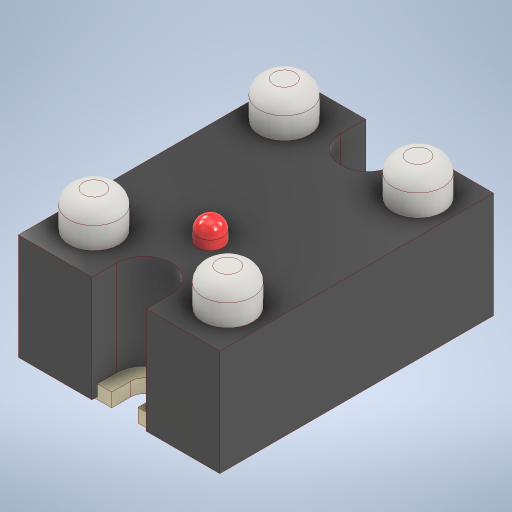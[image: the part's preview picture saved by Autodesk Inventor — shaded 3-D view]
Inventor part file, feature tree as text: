
AUTODESK INVENTOR PART (.ipt)
format: ipt  version: 2023 (Build 270158030, 158C)  size: 387,072 bytes
history: native  units: mm
features: other x4, extrude x4, sketch x4, fillet x2, plane x1, projected_geometry x1
ambient origin geometry x8: Origin, YZ Plane, XZ Plane, XY Plane, X Axis, Y Axis, Z Axis, Center Point
bodies: Body1 (feature_tree), Body2 (feature_tree), Body3 (feature_tree), Body4 (feature_tree)
feature tree (16):
  other  "plate"
  extrude  "Extrusion1"  Depth=26.2mm
  plane  "Work Plane1"
  extrude  "Extrusion2"  Depth=1.9mm TaperAngle=0.0deg
  extrude  "Extrusion3"  Depth=3.64mm
  fillet  "Fillet1"  Radius=3.64mm
  extrude  "Extrusion4"  Depth=36.2mm
  fillet  "Fillet2"  Radius=18.1mm
  sketch  "Sketch1"  dims[d0=36.2mm d1=26.2mm d2=13.1mm]
  sketch  "Sketch2"  dims[d3=18.1mm d4=1.9mm d5=0.0mm]
  projected_geometry  "Projected Loop1"
  other  "case"
  sketch  "Sketch3"  dims[d6=3.64mm d7=2.65mm d8=3.64mm]
  other  "screw-terminals"
  sketch  "Sketch4"  dims[d9=2.65mm d10=36.2mm d11=18.1mm d12=2.65mm d13=-0.4mm d14=0.8mm d15=7.5mm d17=0.8mm d18=0.8mm d20=0.8mm d21=3.75mm d23=7.5mm d24=14.66mm d25=0.0mm d26=4.66mm d27=5.76mm d28=6.94mm d29=4.66mm d30=5.76mm d31=5.0mm d32=0.0mm d33=2.0mm d34=3.5mm d35=12.6mm d36=3.0mm d37=0.0mm d38=1.75mm]
  other  "led"
